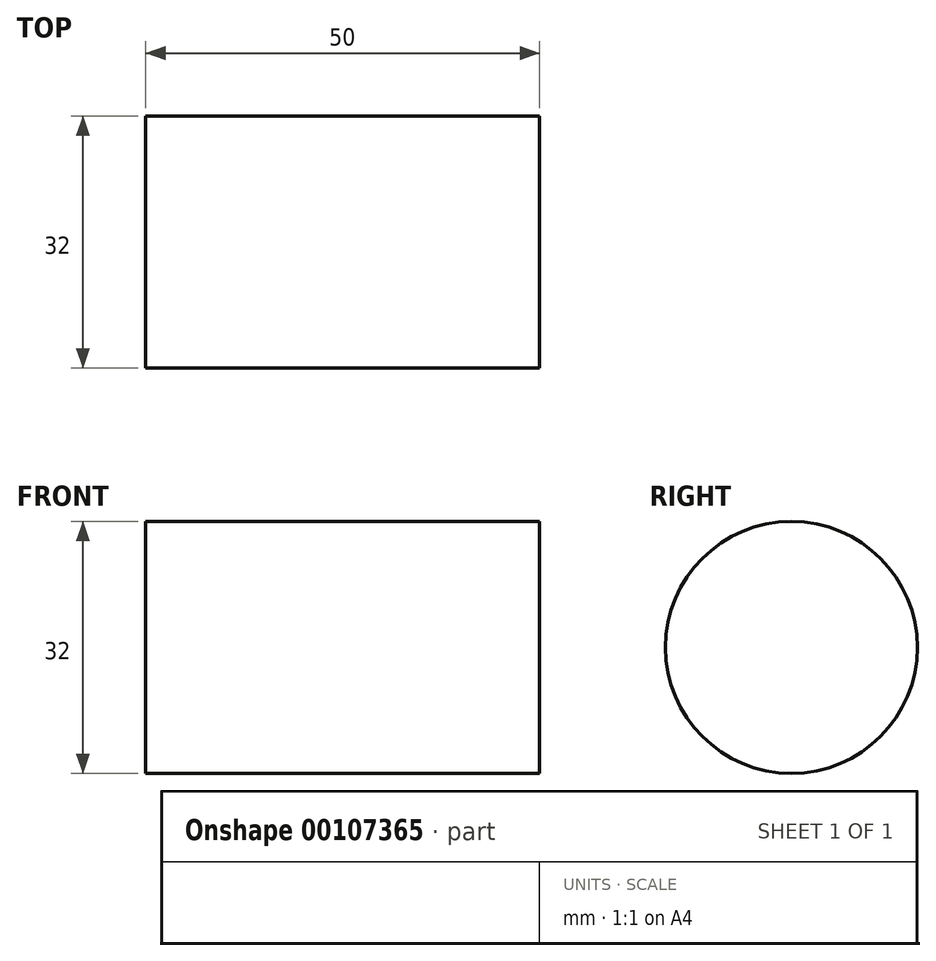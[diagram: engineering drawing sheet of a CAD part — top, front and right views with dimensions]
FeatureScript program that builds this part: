
annotation { "Feature Type Name" : "Feature", "Feature Type Description" : "" }
export const myFeature = defineFeature(function(context is Context, id is Id, definition is map)
    precondition{}
    {
        {
            var Q0;
            Q0=qCreatedBy(makeId("Right.planeOp"),FACE);
            var sketch = newSketch(context, id + "F0", { "sketchPlane" : qUnion([Q0])});
            skCircle(sketch, "E0", {"center": v(0, 0) * mm, "radius": 16 * mm});
            skSolve(sketch);
        }
        {
            var Q0;
            Q0=makeQuery(id+"F0.imprint","IMPRINT",FACE,{"disambiguationData":[TD([[makeQuery(id+"F0.imprint","IMPRINT",EDGE,{"derivedFrom":sQuery(id+"F0.wireOp",EDGE,"E0")}),1.0]])]});
            extrude(context, id + "F1", {"entities" : qUnion([Q0]), "depth" : 25 * mm, "hasSecondDirection" : true, "secondDirectionOppositeDirection" : true, "secondDirectionDepth" : 25 * mm});
        }
    });
